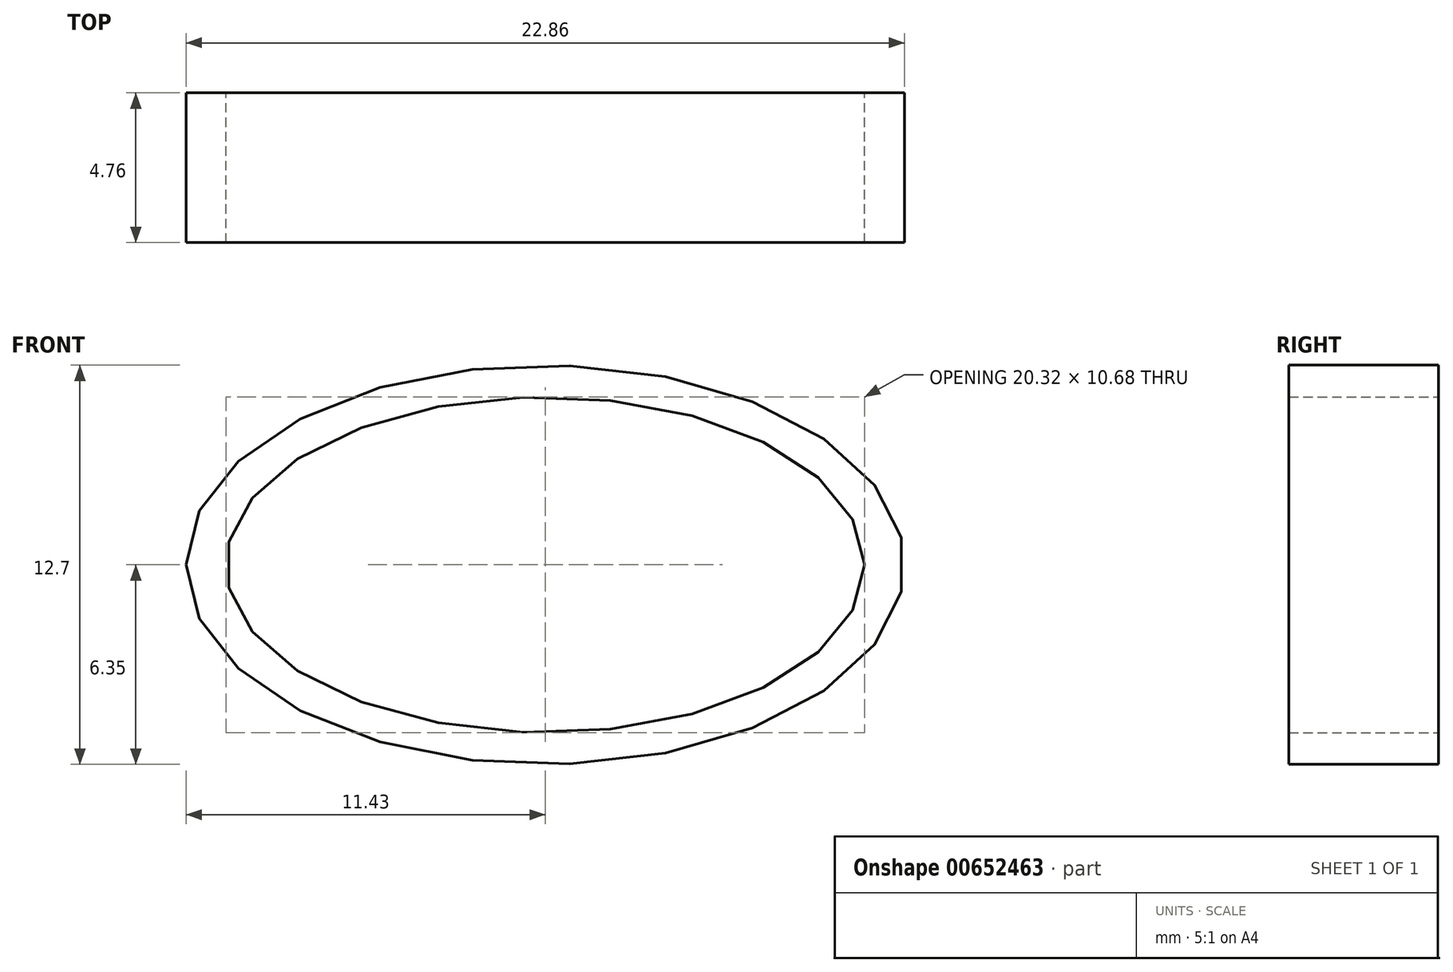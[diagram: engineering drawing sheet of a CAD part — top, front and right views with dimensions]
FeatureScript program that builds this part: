
annotation { "Feature Type Name" : "Feature", "Feature Type Description" : "" }
export const myFeature = defineFeature(function(context is Context, id is Id, definition is map)
    precondition{}
    {
        {
            var Q0;
            Q0=qCreatedBy(makeId("Front.planeOp"),FACE);
            var sketch = newSketch(context, id + "F0", { "sketchPlane" : qUnion([Q0])});
            skEllipse(sketch, "E0", {"center": v(0, 0) * mm, "majorRadius": 11.43 * mm, "minorRadius": 6.35 * mm, "majorAxis": v(-1, 0)});
            skEllipse(sketch, "E1", {"center": v(0, 0) * mm, "majorRadius": 10.16 * mm, "minorRadius": 5.34 * mm, "majorAxis": v(1, 0)});
            skSolve(sketch);
        }
        {
            var Q0;
            Q0 = qSketchRegion(id + "F0", true);
            extrude(context, id + "F1", {"entities" : qUnion([Q0]), "endBound" : BoundingType.SYMMETRIC, "depth" : 4.76 * mm, "offsetDistance" : 25.4 * mm});
        }
    });
